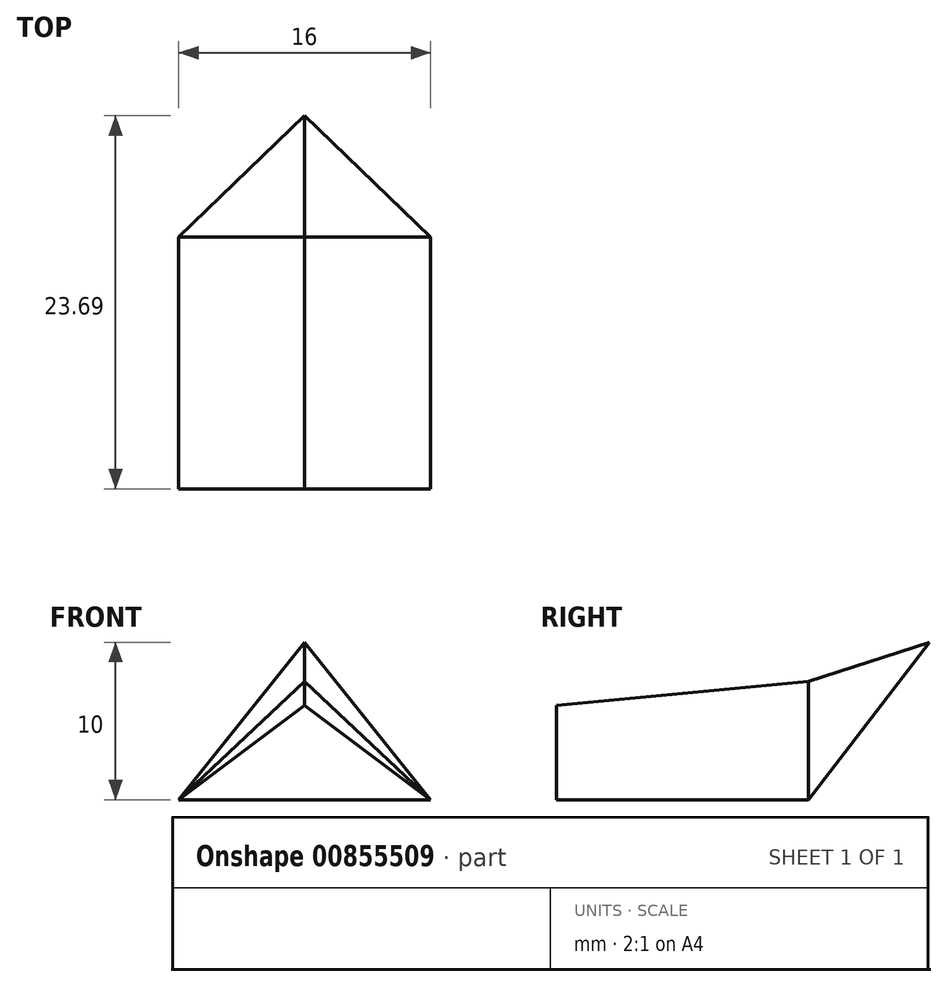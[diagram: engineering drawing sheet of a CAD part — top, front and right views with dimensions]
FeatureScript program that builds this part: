
annotation { "Feature Type Name" : "Feature", "Feature Type Description" : "" }
export const myFeature = defineFeature(function(context is Context, id is Id, definition is map)
    precondition{}
    {
        {
            var Q0;
            Q0=qCreatedBy(makeId("Top.planeOp"),FACE);
            var sketch = newSketch(context, id + "F0", { "sketchPlane" : qUnion([Q0])});
            skLineSegment(sketch, "E0", {"start": v(-25.37, 8) * mm, "end": v(-25.37, -8) * mm});
            skLineSegment(sketch, "E1", {"start": v(0, 0) * mm, "end": v(-11.82, -11.82) * mm, "construction": true});
            skPoint(sketch, "E2", {"position": v(-25.37, 0) * mm});
            skLineSegment(sketch, "E3", {"start": v(-25.37, 8) * mm, "end": v(-30.95, 8) * mm, "construction": true});
            skLineSegment(sketch, "E4", {"start": v(-18.3, 10.93) * mm, "end": v(-10.52, 18.7) * mm});
            skArc(sketch, "E5", {"start": v(-25.37, 8) * mm, "mid": v(-21.54, 8.76) * mm, "end": v(-18.3, 10.93) * mm});
            skLineSegment(sketch, "E6", {"start": v(0, 0) * mm, "end": v(10.07, -10.07) * mm, "construction": true});
            skArc(sketch, "E7.MirrorCS", {"start": v(-8, 25.37) * mm, "mid": v(-8.76, 21.54) * mm, "end": v(-10.93, 18.3) * mm});
            skLineSegment(sketch, "E8.MirrorCS", {"start": v(14.7, 15.65) * mm, "end": v(-1.3, 15.65) * mm});
            skLineSegment(sketch, "E9.MirrorCS", {"start": v(-18.3, -10.93) * mm, "end": v(-10.52, -18.7) * mm});
            skArc(sketch, "E10.MirrorCS", {"start": v(-25.37, 35.4) * mm, "mid": v(-4.94, 31.33) * mm, "end": v(12.39, 19.76) * mm});
            skSolve(sketch);
        }
        {
            var Q0;
            Q0=qCreatedBy(makeId("Front.planeOp"),FACE);
            cPlane(context, id + "F1", {"entities" : qUnion([Q0]), "cplaneType" : CPlaneType.OFFSET, "offset" : 25.37 * mm, "width" : 150 * mm, "height" : 150 * mm});
        }
        {
            var Q0;
            Q0=qCreatedBy(id+"F1.planeOp",FACE);
            cPlane(context, id + "F2", {"entities" : qUnion([Q0]), "cplaneType" : CPlaneType.OFFSET, "offset" : 16 * mm, "width" : 150 * mm, "height" : 150 * mm});
        }
        {
            var Q0;
            Q0=qCreatedBy(id+"F2.planeOp",FACE);
            var sketch = newSketch(context, id + "F3", { "sketchPlane" : qUnion([Q0])});
            skLineSegment(sketch, "E11", {"start": v(-8, 0) * mm, "end": v(8, 0) * mm});
            skLineSegment(sketch, "E12", {"start": v(8, 0) * mm, "end": v(0, 6) * mm});
            skLineSegment(sketch, "E13", {"start": v(0, 6) * mm, "end": v(-8, 0) * mm});
            skSolve(sketch);
        }
        {
            var Q0;
            Q0=qCreatedBy(id+"F1.planeOp",FACE);
            var sketch = newSketch(context, id + "F4", { "sketchPlane" : qUnion([Q0])});
            skLineSegment(sketch, "E14", {"start": v(-8, 0) * mm, "end": v(8, 0) * mm});
            skLineSegment(sketch, "E15", {"start": v(8, 0) * mm, "end": v(0, 7.5) * mm});
            skLineSegment(sketch, "E16", {"start": v(0, 7.5) * mm, "end": v(-8, 0) * mm});
            skSolve(sketch);
        }
        {
            var Q0;
            Q0=qCreatedBy(makeId("Top.planeOp"),FACE);
            cPlane(context, id + "F5", {"entities" : qUnion([Q0]), "cplaneType" : CPlaneType.OFFSET, "offset" : 10 * mm, "width" : 150 * mm, "height" : 150 * mm});
        }
        {
            var Q0;
            Q0=qCreatedBy(id+"F5.planeOp",FACE);
            var sketch = newSketch(context, id + "F6", { "sketchPlane" : qUnion([Q0])});
            skLineSegment(sketch, "E17", {"start": v(0, -17.68) * mm, "end": v(-17.68, 0) * mm});
            skLineSegment(sketch, "E18", {"start": v(-17.68, 0) * mm, "end": v(0, 17.68) * mm});
            skLineSegment(sketch, "E19", {"start": v(0, 17.68) * mm, "end": v(17.68, 0) * mm});
            skLineSegment(sketch, "E20", {"start": v(17.68, 0) * mm, "end": v(0, -17.68) * mm});
            skSolve(sketch);
        }
        {
            var Q0;
            Q0=sQuery(id+"F6.wireOp",VERTEX,"E17.start");
            var Q1;
            Q1=makeQuery(id+"F4.imprint","IMPRINT",FACE,{"disambiguationData":[TD([[makeQuery(id+"F4.imprint","IMPRINT",EDGE,{"derivedFrom":sQuery(id+"F4.wireOp",EDGE,"E14")}),1.0]])]});
            loft(context, id + "F7", {"sheetProfilesArray" : [{ "sheetProfileEntities" : qUnion([Q0]) }, { "sheetProfileEntities" : qUnion([Q1]) }]});
        }
        {
            var Q1;
            Q1=makeQuery(id+"F7.opLoft","CAP_FACE",FACE,{"disambiguationData":[OSD([makeQuery(id+"F4.imprint","IMPRINT",FACE,{"disambiguationData":[TD([[makeQuery(id+"F4.imprint","IMPRINT",EDGE,{"derivedFrom":sQuery(id+"F4.wireOp",EDGE,"E14")}),1.0]])]})])],"isStart":true});
            var Q2;
            Q2=makeQuery(id+"F3.imprint","IMPRINT",FACE,{"disambiguationData":[TD([[makeQuery(id+"F3.imprint","IMPRINT",EDGE,{"derivedFrom":sQuery(id+"F3.wireOp",EDGE,"E11")}),1.0]])]});
            loft(context, id + "F8", {"operationType" : NewBodyOperationType.ADD, "sheetProfilesArray" : [{ "sheetProfileEntities" : qUnion([Q1]) }, { "sheetProfileEntities" : qUnion([Q2]) }]});
        }
    });
